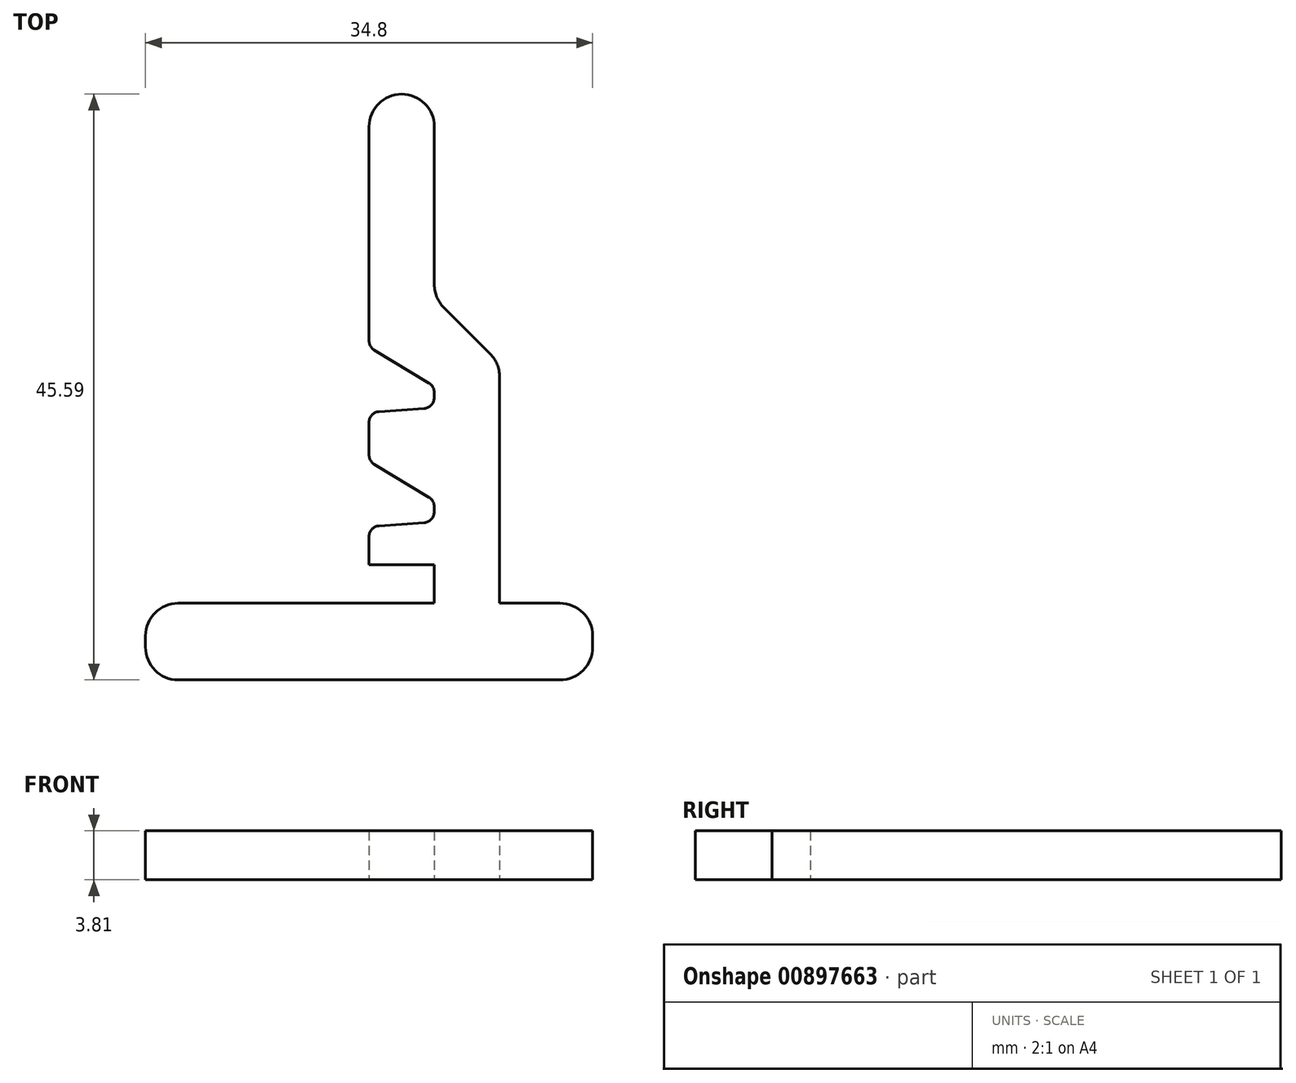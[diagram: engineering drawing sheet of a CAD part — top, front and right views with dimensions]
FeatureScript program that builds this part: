
annotation { "Feature Type Name" : "Feature", "Feature Type Description" : "" }
export const myFeature = defineFeature(function(context is Context, id is Id, definition is map)
    precondition{}
    {
        {
            var Q0;
            Q0=qCreatedBy(makeId("Top.planeOp"),FACE);
            var sketch = newSketch(context, id + "F0", { "sketchPlane" : qUnion([Q0])});
            skLineSegment(sketch, "E0.bottom", {"start": v(0, 0) * mm, "end": v(34.8, 0) * mm});
            skLineSegment(sketch, "E0.top", {"start": v(0, 11.94) * mm, "end": v(34.8, 11.94) * mm});
            skLineSegment(sketch, "E0.left", {"start": v(0, 0) * mm, "end": v(0, 11.94) * mm});
            skLineSegment(sketch, "E0.right", {"start": v(34.8, 0) * mm, "end": v(34.8, 11.94) * mm});
            skLineSegment(sketch, "E1", {"start": v(17.4, 11.94) * mm, "end": v(22.47, 12.3) * mm});
            skLineSegment(sketch, "E2", {"start": v(22.47, 12.3) * mm, "end": v(22.47, 13.97) * mm});
            skLineSegment(sketch, "E3", {"start": v(22.47, 13.97) * mm, "end": v(17.4, 17.02) * mm});
            skPoint(sketch, "E3.endSnap0", {"position": v(17.4, 11.94) * mm});
            skLineSegment(sketch, "E4", {"start": v(17.4, 17.02) * mm, "end": v(17.4, 29.72) * mm});
            skLineSegment(sketch, "E5", {"start": v(17.4, 29.72) * mm, "end": v(22.48, 29.72) * mm});
            skLineSegment(sketch, "E6", {"start": v(22.48, 29.72) * mm, "end": v(27.56, 24.64) * mm});
            skLineSegment(sketch, "E7", {"start": v(27.56, 24.64) * mm, "end": v(27.56, 11.94) * mm});
            skPoint(sketch, "E8.endSnap0", {"position": v(0, 5.97) * mm});
            skLineSegment(sketch, "E9", {"start": v(17.4, 17.02) * mm, "end": v(17.4, 11.94) * mm});
            skLineSegment(sketch, "E10", {"start": v(17.4, 20.83) * mm, "end": v(22.47, 21.18) * mm});
            skLineSegment(sketch, "E11", {"start": v(22.47, 21.18) * mm, "end": v(22.47, 22.86) * mm});
            skLineSegment(sketch, "E12", {"start": v(22.47, 22.86) * mm, "end": v(17.4, 25.9) * mm});
            skLineSegment(sketch, "E13", {"start": v(17.4, 29.72) * mm, "end": v(17.4, 45.6) * mm});
            skLineSegment(sketch, "E14", {"start": v(17.4, 45.6) * mm, "end": v(22.48, 45.6) * mm});
            skLineSegment(sketch, "E15", {"start": v(22.48, 45.6) * mm, "end": v(22.48, 29.72) * mm});
            skLineSegment(sketch, "E16", {"start": v(0, 5.97) * mm, "end": v(22.47, 5.97) * mm});
            skLineSegment(sketch, "E17", {"start": v(22.47, 5.97) * mm, "end": v(22.47, 8.95) * mm});
            skLineSegment(sketch, "E18", {"start": v(22.47, 8.95) * mm, "end": v(17.4, 8.95) * mm});
            skLineSegment(sketch, "E19", {"start": v(17.4, 8.95) * mm, "end": v(17.4, 11.94) * mm});
            skLineSegment(sketch, "E20", {"start": v(27.56, 11.94) * mm, "end": v(27.56, 5.97) * mm});
            skLineSegment(sketch, "E21", {"start": v(27.56, 5.97) * mm, "end": v(34.8, 5.97) * mm});
            skSolve(sketch);
        }
        {
            var Q0;
            {var subQ7=sQuery(id+"F0.wireOp",EDGE,"E1");Q0=makeQuery(id+"F0.imprint","IMPRINT",FACE,{"disambiguationData":[TD([[makeQuery(id+"F0.imprint","IMPRINT",EDGE,{"derivedFrom":subQ7}),-1.0]])]});}
            var Q1;
            {var subQ1=sQuery(id+"F0.wireOp",EDGE,"E0.bottom");Q1=makeQuery(id+"F0.imprint","IMPRINT",FACE,{"disambiguationData":[TD([[makeQuery(id+"F0.imprint","IMPRINT",EDGE,{"derivedFrom":subQ1}),1.0]])]});}
            var Q2;
            Q2=makeQuery(id+"F0.imprint","IMPRINT",FACE,{"disambiguationData":[TD([[makeQuery(id+"F0.imprint","IMPRINT",EDGE,{"derivedFrom":sQuery(id+"F0.wireOp",EDGE,"E5")}),1.0]])]});
            extrude(context, id + "F1", {"entities" : qUnion([Q0, Q1, Q2]), "depth" : 3.8 * mm, "offsetDistance" : 25.4 * mm});
        }
        {
            var Q0;
            Q0=makeQuery(id+"F1.opExtrude","SWEPT_EDGE",EDGE,{"disambiguationData":[OSD([sQuery(id+"F0.wireOp",EDGE,"E0.left"),sQuery(id+"F0.wireOp",EDGE,"2ySY6fz7-6k90-h9BO-5PrX-0AQ8x13uOmU0")])]});
            var Q1;
            Q1=makeQuery(id+"F1.opExtrude","SWEPT_EDGE",EDGE,{"disambiguationData":[OSD([sQuery(id+"F0.wireOp",EDGE,"E0.bottom"),sQuery(id+"F0.wireOp",EDGE,"E0.left")])]});
            var Q2;
            Q2=makeQuery(id+"F1.opExtrude","SWEPT_EDGE",EDGE,{"disambiguationData":[OSD([sQuery(id+"F0.wireOp",EDGE,"E0.right"),sQuery(id+"F0.wireOp",EDGE,"aAzFGL1Z-sAIC-5Xnu-Zft4-2NqlRH4mAx22")])]});
            var Q3;
            Q3=makeQuery(id+"F1.opExtrude","SWEPT_EDGE",EDGE,{"disambiguationData":[OSD([sQuery(id+"F0.wireOp",EDGE,"E0.bottom"),sQuery(id+"F0.wireOp",EDGE,"E0.right")])]});
            var Q4;
            Q4=makeQuery(id+"F1.opExtrude","SWEPT_EDGE",EDGE,{"disambiguationData":[OSD([sQuery(id+"F0.wireOp",EDGE,"E8"),sQuery(id+"F0.wireOp",EDGE,"2ySY6fz7-6k90-h9BO-5PrX-0AQ8x13uOmU0")])]});
            var Q5;
            Q5=makeQuery(id+"F1.opExtrude","SWEPT_EDGE",EDGE,{"disambiguationData":[OSD([sQuery(id+"F0.wireOp",EDGE,"3UoZxhjQ-1YX1-oY9f-wCgj-dJ6USQsgY59g"),sQuery(id+"F0.wireOp",EDGE,"aAzFGL1Z-sAIC-5Xnu-Zft4-2NqlRH4mAx22")])]});
            var Q6;
            Q6=makeQuery(id+"F1.opExtrude","SWEPT_EDGE",EDGE,{"disambiguationData":[OSD([sQuery(id+"F0.wireOp",EDGE,"E13"),sQuery(id+"F0.wireOp",EDGE,"E14")])]});
            var Q7;
            Q7=makeQuery(id+"F1.opExtrude","SWEPT_EDGE",EDGE,{"disambiguationData":[OSD([sQuery(id+"F0.wireOp",EDGE,"E14"),sQuery(id+"F0.wireOp",EDGE,"E15")])]});
            fillet(context, id + "F2", {"entities" : qUnion([Q0, Q1, Q2, Q3, Q4, Q5, Q6, Q7]), "radius" : 2.54 * mm, "tangentPropagation" : true, "allowEdgeOverflow" : false});
        }
        {
            var Q0;
            Q0=makeQuery(id+"F1.opExtrude","SWEPT_EDGE",EDGE,{"disambiguationData":[OSD([sQuery(id+"F0.wireOp",EDGE,"E10"),sQuery(id+"F0.wireOp",EDGE,"E11")])]});
            var Q1;
            Q1=makeQuery(id+"F1.opExtrude","SWEPT_EDGE",EDGE,{"disambiguationData":[OSD([sQuery(id+"F0.wireOp",EDGE,"E11"),sQuery(id+"F0.wireOp",EDGE,"E12")])]});
            var Q2;
            Q2=makeQuery(id+"F1.opExtrude","SWEPT_EDGE",EDGE,{"disambiguationData":[OSD([sQuery(id+"F0.wireOp",EDGE,"E1"),sQuery(id+"F0.wireOp",EDGE,"E2")])]});
            var Q3;
            Q3=makeQuery(id+"F1.opExtrude","SWEPT_EDGE",EDGE,{"disambiguationData":[OSD([sQuery(id+"F0.wireOp",EDGE,"E2"),sQuery(id+"F0.wireOp",EDGE,"E3")])]});
            var Q4;
            Q4=makeQuery(id+"F1.opExtrude","SWEPT_EDGE",EDGE,{"disambiguationData":[OSD([sQuery(id+"F0.wireOp",EDGE,"E0.top"),sQuery(id+"F0.wireOp",EDGE,"E1"),sQuery(id+"F0.wireOp",EDGE,"E8"),sQuery(id+"F0.wireOp",EDGE,"E9")])]});
            var Q5;
            Q5=makeQuery(id+"F1.opExtrude","SWEPT_EDGE",EDGE,{"disambiguationData":[OSD([sQuery(id+"F0.wireOp",EDGE,"E3"),sQuery(id+"F0.wireOp",EDGE,"E4"),sQuery(id+"F0.wireOp",EDGE,"E9")])]});
            var Q6;
            Q6=makeQuery(id+"F1.opExtrude","SWEPT_EDGE",EDGE,{"disambiguationData":[OSD([sQuery(id+"F0.wireOp",EDGE,"E4"),sQuery(id+"F0.wireOp",EDGE,"E10")])]});
            var Q7;
            Q7=makeQuery(id+"F1.opExtrude","SWEPT_EDGE",EDGE,{"disambiguationData":[OSD([sQuery(id+"F0.wireOp",EDGE,"E4"),sQuery(id+"F0.wireOp",EDGE,"E12")])]});
            fillet(context, id + "F3", {"entities" : qUnion([Q0, Q1, Q2, Q3, Q4, Q5, Q6, Q7]), "radius" : 0.84 * mm, "tangentPropagation" : true, "allowEdgeOverflow" : false});
        }
        {
            var Q0;
            Q0=makeQuery(id+"F1.opExtrude","SWEPT_EDGE",EDGE,{"disambiguationData":[OSD([sQuery(id+"F0.wireOp",EDGE,"E4"),sQuery(id+"F0.wireOp",EDGE,"E5")])]});
            var Q1;
            Q1=makeQuery(id+"F1.opExtrude","SWEPT_EDGE",EDGE,{"disambiguationData":[OSD([sQuery(id+"F0.wireOp",EDGE,"E5"),sQuery(id+"F0.wireOp",EDGE,"E6")])]});
            var Q2;
            Q2=makeQuery(id+"F1.opExtrude","SWEPT_EDGE",EDGE,{"disambiguationData":[OSD([sQuery(id+"F0.wireOp",EDGE,"E6"),sQuery(id+"F0.wireOp",EDGE,"E7")])]});
            var Q3;
            Q3=makeQuery(id+"F1.opExtrude","SWEPT_EDGE",EDGE,{"disambiguationData":[OSD([sQuery(id+"F0.wireOp",EDGE,"E0.top"),sQuery(id+"F0.wireOp",EDGE,"E7"),sQuery(id+"F0.wireOp",EDGE,"3UoZxhjQ-1YX1-oY9f-wCgj-dJ6USQsgY59g")])]});
            fillet(context, id + "F4", {"entities" : qUnion([Q0, Q1, Q2, Q3]), "radius" : 2.54 * mm, "tangentPropagation" : true, "allowEdgeOverflow" : false});
        }
    });
